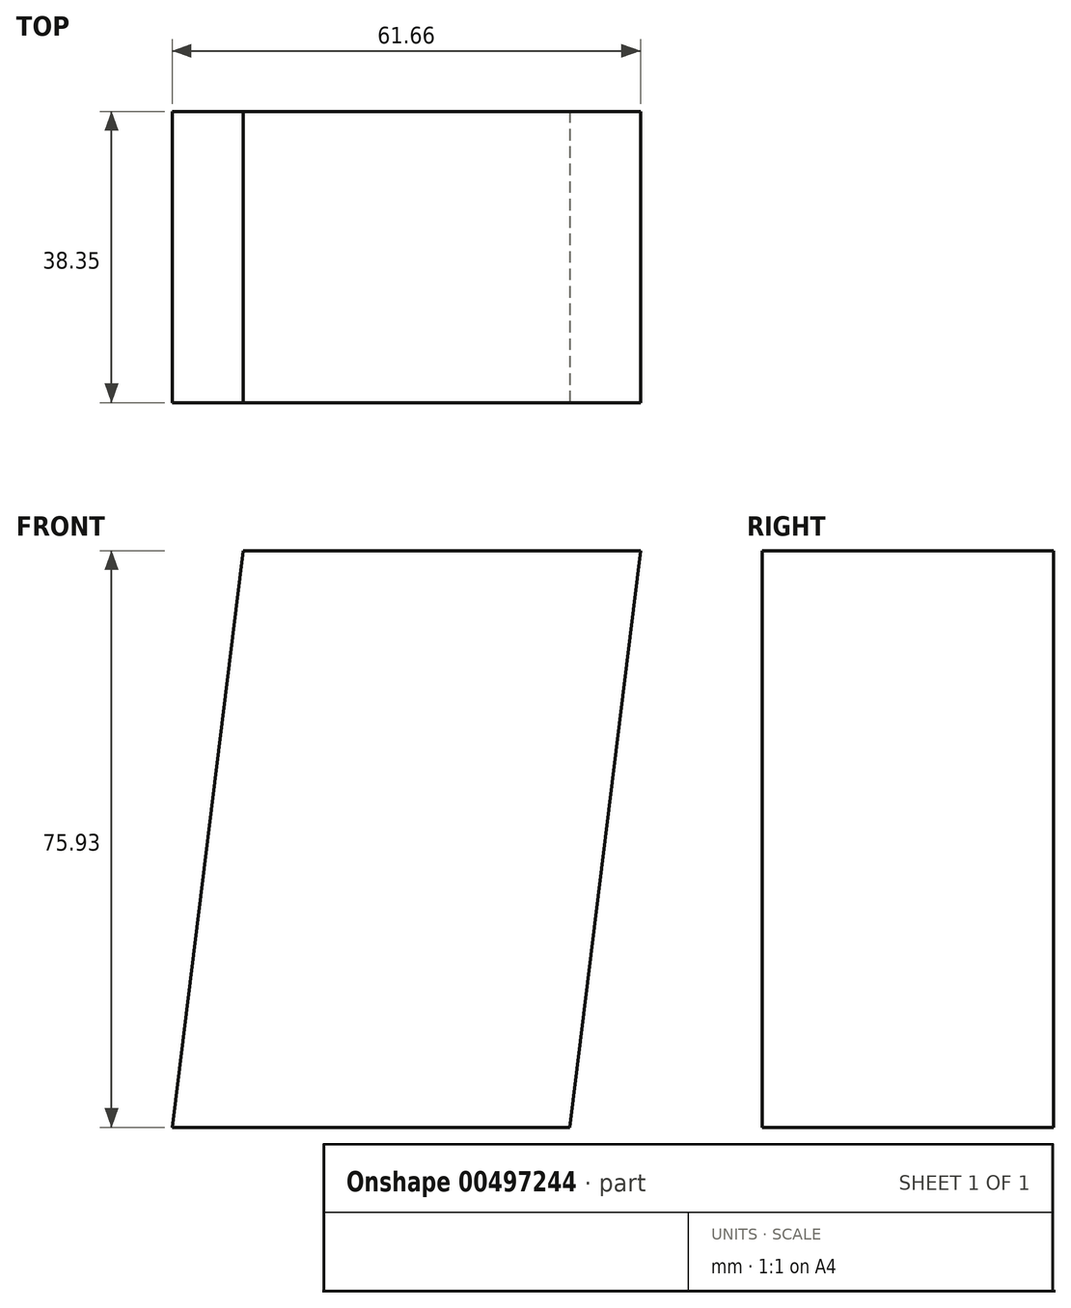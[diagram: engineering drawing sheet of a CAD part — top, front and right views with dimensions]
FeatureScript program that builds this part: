
annotation { "Feature Type Name" : "Feature", "Feature Type Description" : "" }
export const myFeature = defineFeature(function(context is Context, id is Id, definition is map)
    precondition{}
    {
        {
            var Q0;
            Q0=qCreatedBy(makeId("Front.planeOp"),FACE);
            var sketch = newSketch(context, id + "F0", { "sketchPlane" : qUnion([Q0])});
            skLineSegment(sketch, "E0", {"start": v(-37.81, -38.6) * mm, "end": v(-29.27, 31.01) * mm});
            skLineSegment(sketch, "E1", {"start": v(23.07, 31.01) * mm, "end": v(13.74, -44.92) * mm});
            skLineSegment(sketch, "E2", {"start": v(-37.81, -38.6) * mm, "end": v(-38.6, -44.92) * mm});
            skLineSegment(sketch, "E3", {"start": v(13.74, -44.92) * mm, "end": v(-38.6, -44.92) * mm});
            skLineSegment(sketch, "E4", {"start": v(23.07, 31.01) * mm, "end": v(-29.27, 31.01) * mm});
            skSolve(sketch);
        }
        {
            var Q0;
            Q0 = qSketchRegion(id + "F0", true);
            extrude(context, id + "F1", {"entities" : qUnion([Q0]), "oppositeDirection" : true, "depth" : 38.35 * mm});
        }
    });
